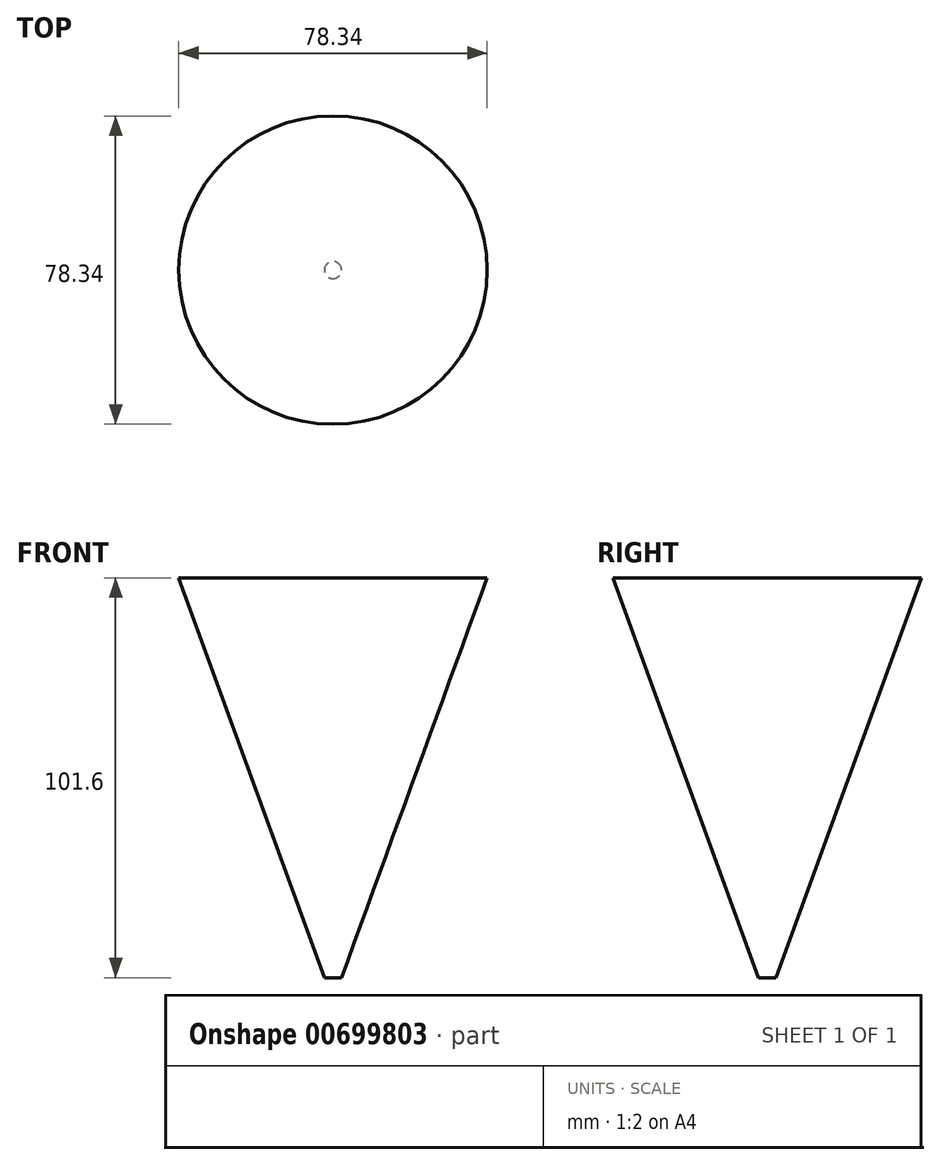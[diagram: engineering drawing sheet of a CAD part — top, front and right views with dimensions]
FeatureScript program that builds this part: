
annotation { "Feature Type Name" : "Feature", "Feature Type Description" : "" }
export const myFeature = defineFeature(function(context is Context, id is Id, definition is map)
    precondition{}
    {
        {
            var Q0;
            Q0=qCreatedBy(makeId("Top.planeOp"),FACE);
            var sketch = newSketch(context, id + "F0", { "sketchPlane" : qUnion([Q0])});
            skCircle(sketch, "E0", {"center": v(0, 0) * mm, "radius": 2.2 * mm});
            skSolve(sketch);
        }
        {
            var Q0;
            Q0=makeQuery(id+"F0.imprint","IMPRINT",FACE,{"disambiguationData":[TD([[makeQuery(id+"F0.imprint","IMPRINT",EDGE,{"derivedFrom":sQuery(id+"F0.wireOp",EDGE,"E0")}),1.0]])]});
            extrude(context, id + "F1", {"entities" : qUnion([Q0]), "depth" : 101.6 * mm, "offsetDistance" : 25.4 * mm, "hasDraft" : true, "draftAngle" : 20 * degree});
        }
    });
